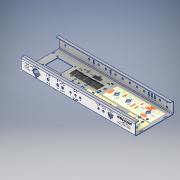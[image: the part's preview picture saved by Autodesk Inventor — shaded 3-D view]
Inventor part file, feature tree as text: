
AUTODESK INVENTOR PART (.ipt)
format: ipt  version: 2018.3 (Build 223284000, 284)  size: 2,821,120 bytes
history: native  units: in
note: dims shown in document units (in); Inventor stores cm internally (conversion verified against a paired STEP export)
features: other x24, sheet_metal_op x13, sketch x10
ambient origin geometry x8: Origin, YZ Plane, XZ Plane, XY Plane, X Axis, Y Axis, Z Axis, Center Point
bodies: Solid1 (feature_tree)
feature tree (47):
  sheet_metal_op  "Face1"
  sketch  "Sketch2"  dims[d0=23.75in]
  sheet_metal_op  "Flange1"
  sheet_metal_op  "Flange2"
  sheet_metal_op  "Flange3"
  sheet_metal_op  "Flange4"
  other  "Decal1"
  other  "Decal2"
  sketch  "Sketch11"  dims[d12=0.5in d13=0.125in d14=0.125in d17=0.125in d18=0.0625in d19=0.25in d20=0.125in d21=0.75in d22=90.0deg d23=0.125in d24=0.5in d25=0.125in d26=0.125in d27=0.125in d28=0.0in d29=0.125in d30=0.0625in d31=0.25in d32=0.125in d33=2.5in d34=90.0deg d35=0.125in d36=0.5in d37=0.125in d38=0.125in d39=0.125in d40=0.0625in d41=0.25in d42=0.125in d43=0.75in d44=90.0deg d45=0.125in d46=0.5in d47=0.125in d48=0.125in d49=0.125in d50=0.0in d353=1.181in d378=0.13in d379=0.13in d417=0.9in d418=0.9in]
  other  "Decal3"
  other  "Decal4"
  other  "Decal5"
  other  "Decal6"
  other  "Plate1"
  sketch  "Sketch3"  dims[d1=8.05in]
  other  "Plate2"
  sheet_metal_op  "Bend1"
  sheet_metal_op  "Corner1"
  sketch  "Sketch4"  dims[d2=0.125in]
  other  "Plate3"
  sheet_metal_op  "Bend2"
  sheet_metal_op  "Corner2"
  sketch  "Sketch5"  dims[d3=0.125in]
  sketch  "Sketch6"  dims[d4=0.0in d5=0.125in]
  other  "Plate4"
  sheet_metal_op  "Bend3"
  sheet_metal_op  "Corner3"
  sketch  "Sketch7"  dims[d6=0.0625in]
  other  "Plate5"
  sheet_metal_op  "Bend4"
  sheet_metal_op  "Corner4"
  sketch  "Sketch8"  dims[d7=0.25in]
  sketch  "Sketch9"  dims[d8=0.125in]
  sketch  "Sketch10"  dims[d9=2.5in d10=90.0deg d11=0.125in]
  other  "Image6"
  other  "Image7"
  other  "Image8"
  other  "Image9"
  other  "Image10"
  other  "Image12"
  other  "Image13"
  other  "Image15"
  other  "Image16"
  other  "Cut1"
  other  "Cut2"
  other  "Cut3"
  other  "Definition1"
